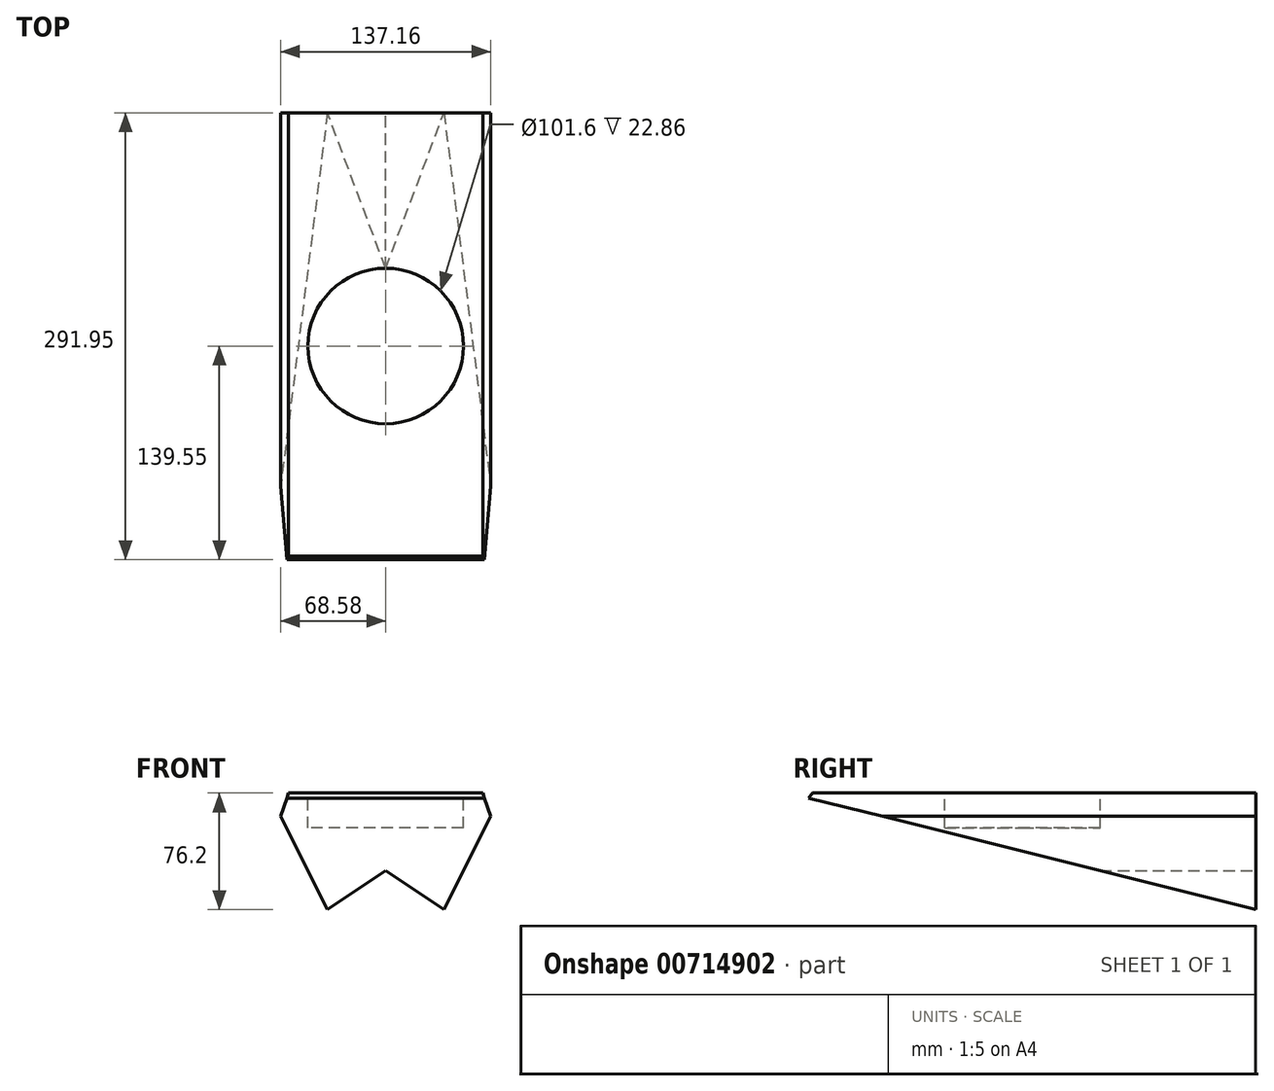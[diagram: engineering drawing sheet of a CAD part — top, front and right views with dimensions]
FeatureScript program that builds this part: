
annotation { "Feature Type Name" : "Feature", "Feature Type Description" : "" }
export const myFeature = defineFeature(function(context is Context, id is Id, definition is map)
    precondition{}
    {
        {
            var Q0;
            Q0=qCreatedBy(makeId("Front.planeOp"),FACE);
            var sketch = newSketch(context, id + "F0", { "sketchPlane" : qUnion([Q0])});
            skLineSegment(sketch, "E0.bottom", {"start": v(0, 0) * mm, "end": v(-152.4, 0) * mm});
            skLineSegment(sketch, "E0.top", {"start": v(0, 76.2) * mm, "end": v(-152.4, 76.2) * mm});
            skLineSegment(sketch, "E0.left", {"start": v(0, 0) * mm, "end": v(0, 76.2) * mm});
            skLineSegment(sketch, "E0.right", {"start": v(-152.4, 0) * mm, "end": v(-152.4, 76.2) * mm});
            skSolve(sketch);
        }
        {
            var Q0;
            Q0 = qSketchRegion(id + "F0", true);
            extrude(context, id + "F1", {"entities" : qUnion([Q0]), "depth" : 304.8 * mm, "offsetDistance" : 25.4 * mm});
        }
        {
            var Q0;
            Q0=qCreatedBy(makeId("Right.planeOp"),FACE);
            var sketch = newSketch(context, id + "F2", { "sketchPlane" : qUnion([Q0])});
            skLineSegment(sketch, "E1", {"start": v(0, 0) * mm, "end": v(-304.8, 0) * mm});
            skLineSegment(sketch, "E2", {"start": v(-304.8, 0) * mm, "end": v(-304.8, 76.2) * mm});
            skLineSegment(sketch, "E3", {"start": v(-304.8, 76.2) * mm, "end": v(0, 0) * mm});
            skSolve(sketch);
        }
        {
            var Q0;
            Q0 = qSketchRegion(id + "F2", true);
            extrude(context, id + "F3", {"entities" : qUnion([Q0]), "operationType" : NewBodyOperationType.REMOVE, "oppositeDirection" : true, "depth" : 304.8 * mm, "offsetDistance" : 25.4 * mm});
        }
        {
            var Q0;
            Q0=qCreatedBy(makeId("Front.planeOp"),FACE);
            var sketch = newSketch(context, id + "F4", { "sketchPlane" : qUnion([Q0])});
            skLineSegment(sketch, "E4", {"start": v(0, 0) * mm, "end": v(-38.1, 0) * mm});
            skLineSegment(sketch, "E5", {"start": v(0, 0) * mm, "end": v(0, 76.2) * mm});
            skLineSegment(sketch, "E6", {"start": v(0, 76.2) * mm, "end": v(-38.1, 0) * mm});
            skSolve(sketch);
        }
        {
            var Q0;
            Q0 = qSketchRegion(id + "F4", true);
            extrude(context, id + "F5", {"entities" : qUnion([Q0]), "operationType" : NewBodyOperationType.REMOVE, "oppositeDirection" : true, "depth" : -304.8 * mm, "offsetDistance" : 25.4 * mm});
        }
        {
            var Q0;
            Q0=qCreatedBy(makeId("Front.planeOp"),FACE);
            var sketch = newSketch(context, id + "F6", { "sketchPlane" : qUnion([Q0])});
            skLineSegment(sketch, "E7", {"start": v(0, 0) * mm, "end": v(-152.4, 0) * mm});
            skLineSegment(sketch, "E8", {"start": v(-152.4, 0) * mm, "end": v(-114.3, 0) * mm});
            skLineSegment(sketch, "E9", {"start": v(-152.4, 0) * mm, "end": v(-152.4, 76.2) * mm});
            skLineSegment(sketch, "E10", {"start": v(-152.4, 76.2) * mm, "end": v(-114.3, 0) * mm});
            skSolve(sketch);
        }
        {
            var Q0;
            Q0 = qSketchRegion(id + "F6", true);
            extrude(context, id + "F7", {"entities" : qUnion([Q0]), "operationType" : NewBodyOperationType.REMOVE, "depth" : 304.8 * mm, "offsetDistance" : 25.4 * mm});
        }
        {
            var Q0;
            Q0=qCreatedBy(makeId("Right.planeOp"),FACE);
            var sketch = newSketch(context, id + "F8", { "sketchPlane" : qUnion([Q0])});
            skLineSegment(sketch, "E11", {"start": v(0, 0) * mm, "end": v(-304.8, 0) * mm});
            skLineSegment(sketch, "E12", {"start": v(-304.8, 0) * mm, "end": v(-304.8, 76.2) * mm});
            skLineSegment(sketch, "E13", {"start": v(-304.8, 76.2) * mm, "end": v(-289.56, 76.2) * mm});
            skLineSegment(sketch, "E14", {"start": v(-289.56, 76.2) * mm, "end": v(-304.8, 55.72) * mm});
            skSolve(sketch);
        }
        {
            var Q0;
            Q0 = qSketchRegion(id + "F8", true);
            extrude(context, id + "F9", {"entities" : qUnion([Q0]), "operationType" : NewBodyOperationType.REMOVE, "oppositeDirection" : true, "depth" : 304.8 * mm, "offsetDistance" : 25.4 * mm});
        }
        {
            var Q0;
            Q0=qCreatedBy(makeId("Front.planeOp"),FACE);
            var sketch = newSketch(context, id + "F10", { "sketchPlane" : qUnion([Q0])});
            skLineSegment(sketch, "E15", {"start": v(0, 0) * mm, "end": v(0, 76.2) * mm});
            skLineSegment(sketch, "E16", {"start": v(0, 76.2) * mm, "end": v(-12.7, 76.2) * mm});
            skLineSegment(sketch, "E17", {"start": v(-12.7, 76.2) * mm, "end": v(0, 38.1) * mm});
            skSolve(sketch);
        }
        {
            var Q0;
            Q0 = qSketchRegion(id + "F10", true);
            extrude(context, id + "F11", {"entities" : qUnion([Q0]), "operationType" : NewBodyOperationType.REMOVE, "oppositeDirection" : true, "depth" : -304.8 * mm, "offsetDistance" : 25.4 * mm});
        }
        {
            var Q0;
            Q0=qCreatedBy(makeId("Front.planeOp"),FACE);
            var sketch = newSketch(context, id + "F12", { "sketchPlane" : qUnion([Q0])});
            skLineSegment(sketch, "E18", {"start": v(0, 0) * mm, "end": v(-152.4, 0) * mm});
            skLineSegment(sketch, "E19", {"start": v(-152.4, 0) * mm, "end": v(-152.4, 76.2) * mm});
            skLineSegment(sketch, "E20", {"start": v(-152.4, 76.2) * mm, "end": v(-139.7, 76.2) * mm});
            skLineSegment(sketch, "E21", {"start": v(-139.7, 76.2) * mm, "end": v(-152.4, 38.1) * mm});
            skSolve(sketch);
        }
        {
            var Q0;
            Q0 = qSketchRegion(id + "F12", true);
            extrude(context, id + "F13", {"entities" : qUnion([Q0]), "operationType" : NewBodyOperationType.REMOVE, "oppositeDirection" : true, "depth" : -304.8 * mm, "offsetDistance" : 25.4 * mm});
        }
        {
            var Q0;
            Q0=qCreatedBy(makeId("Front.planeOp"),FACE);
            var sketch = newSketch(context, id + "F14", { "sketchPlane" : qUnion([Q0])});
            skLineSegment(sketch, "E22", {"start": v(0, 0) * mm, "end": v(-152.4, 0) * mm});
            skLineSegment(sketch, "E23", {"start": v(0, 0) * mm, "end": v(-76.2, 0) * mm});
            skLineSegment(sketch, "E24", {"start": v(-76.2, 0) * mm, "end": v(-76.2, 25.4) * mm});
            skLineSegment(sketch, "E25", {"start": v(0, 0) * mm, "end": v(-38.1, 0) * mm});
            skLineSegment(sketch, "E26", {"start": v(-38.1, 0) * mm, "end": v(-114.3, 0) * mm});
            skLineSegment(sketch, "E27", {"start": v(-38.1, 0) * mm, "end": v(-76.2, 25.4) * mm});
            skLineSegment(sketch, "E28", {"start": v(-114.3, 0) * mm, "end": v(-76.2, 25.4) * mm});
            skSolve(sketch);
        }
        {
            var Q0;
            Q0 = qSketchRegion(id + "F14", true);
            extrude(context, id + "F15", {"entities" : qUnion([Q0]), "operationType" : NewBodyOperationType.REMOVE, "oppositeDirection" : true, "depth" : -304.8 * mm, "offsetDistance" : 25.4 * mm});
        }
        {
            var Q0;
            Q0=makeQuery(id+"F1.opExtrude","SWEPT_FACE",FACE,{"disambiguationData":[OSD([sQuery(id+"F0.wireOp",EDGE,"E0.top")])]});
            var sketch = newSketch(context, id + "F16", { "sketchPlane" : qUnion([Q0])});
            skCircle(sketch, "E29", {"center": v(-76.2, -152.4) * mm, "radius": 50.8 * mm});
            skSolve(sketch);
        }
        {
            var Q0;
            Q0 = qSketchRegion(id + "F16", true);
            extrude(context, id + "F17", {"entities" : qUnion([Q0]), "operationType" : NewBodyOperationType.REMOVE, "oppositeDirection" : true, "depth" : 22.86 * mm, "offsetDistance" : 25.4 * mm});
        }
    });
